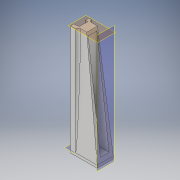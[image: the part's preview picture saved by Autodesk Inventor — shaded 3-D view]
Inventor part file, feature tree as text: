
AUTODESK INVENTOR PART (.ipt)
format: ipt  version: 2019 (Build 230136000, 136)  size: 198,144 bytes
history: native  units: in
note: dims shown in document units (in); Inventor stores cm internally (conversion verified against a paired STEP export)
features: sketch x5, plane x3, extrude x3, loft x1, fillet x1, projected_geometry x1
ambient origin geometry x8: Origin, YZ Plane, XZ Plane, XY Plane, X Axis, Y Axis, Z Axis, Center Point
bodies: Body1 (feature_tree)
feature tree (14):
  sketch  "Sketch5"  dims[d42=1.5in d48=10.0in]
  plane  "Work Plane1"
  loft  "Loft2"
  sketch  "Sketch7"  dims[d58=2.025in d59=0.0in d60=90.0deg d61=0.0in d62=90.0deg]
  plane  "Work Plane2"
  plane  "Work Plane3"
  extrude  "Extrusion10"  Depth=0.25in
  extrude  "Extrusion11"  TaperAngle=0.0deg  [1 undecoded]
  fillet  "Fillet2"  [1 undecoded]
  extrude  "Extrusion12"  Depth=0.324in
  sketch  "Sketch6"  dims[d51=1.0in d52=0.8in d53=0.25in]
  sketch  "Sketch10"  dims[d63=0.475in d64=0.324in]
  projected_geometry  "Projected Loop3"
  sketch  "Sketch11"  dims[d67=0.238in d68=0.225in d69=0.355in d70=0.79in d71=2.125in d72=2.313in d73=0.187in d74=0.187in d81=0.252in d82=0.0in d83=0.252in d84=0.0in d85=0.25in d86=0.815in d87=0.3425in d88=1.5in d89=0.7in d90=1.25in d91=0.0in]
note: 2 required parameter values undecoded (feature->parameter linkage not recoverable at this tier; creation-order binding heuristic only, values carry confidence <= 0.55)
